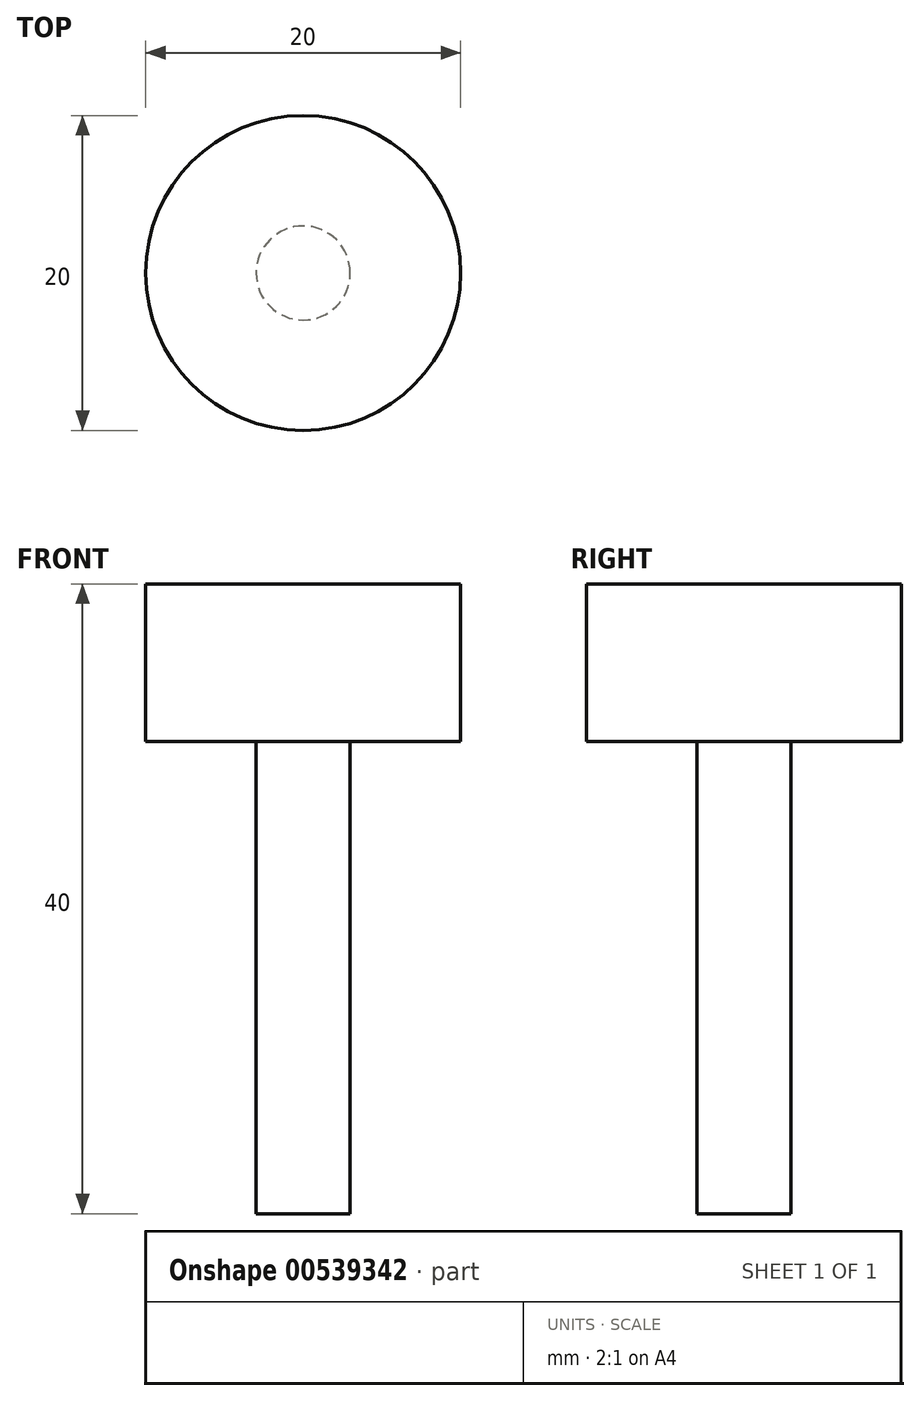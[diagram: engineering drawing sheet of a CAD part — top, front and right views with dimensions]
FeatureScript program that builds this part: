
annotation { "Feature Type Name" : "Feature", "Feature Type Description" : "" }
export const myFeature = defineFeature(function(context is Context, id is Id, definition is map)
    precondition{}
    {
        {
            var Q0;
            Q0=qCreatedBy(makeId("Top.planeOp"),FACE);
            var sketch = newSketch(context, id + "F0", { "sketchPlane" : qUnion([Q0]), "disableImprinting" : false});
            skCircle(sketch, "E0", {"center": v(0, 0) * mm, "radius": 3 * mm});
            skSolve(sketch);
        }
        {
            var Q0;
            Q0 = qSketchRegion(id + "F0", true);
            extrude(context, id + "F1", {"entities" : qUnion([Q0]), "flatOperationType" : FlatOperationType.REMOVE, "depth" : 30 * mm, "offsetDistance" : 25 * mm, "domain" : OperationDomain.MODEL});
        }
        {
            var Q0;
            Q0=makeQuery(id+"F1.opExtrude","CAP_FACE",FACE,{"disambiguationData":[OSD([sQuery(id+"F0.wireOp",EDGE,"E0")])],"isStart":false});
            var sketch = newSketch(context, id + "F2", { "sketchPlane" : qUnion([Q0])});
            skCircle(sketch, "E1", {"center": v(0, 0) * mm, "radius": 10 * mm});
            skSolve(sketch);
        }
        {
            var Q0;
            Q0 = qSketchRegion(id + "F2", true);
            extrude(context, id + "F3", {"entities" : qUnion([Q0]), "operationType" : NewBodyOperationType.ADD, "depth" : 10 * mm, "offsetDistance" : 25 * mm});
        }
    });
